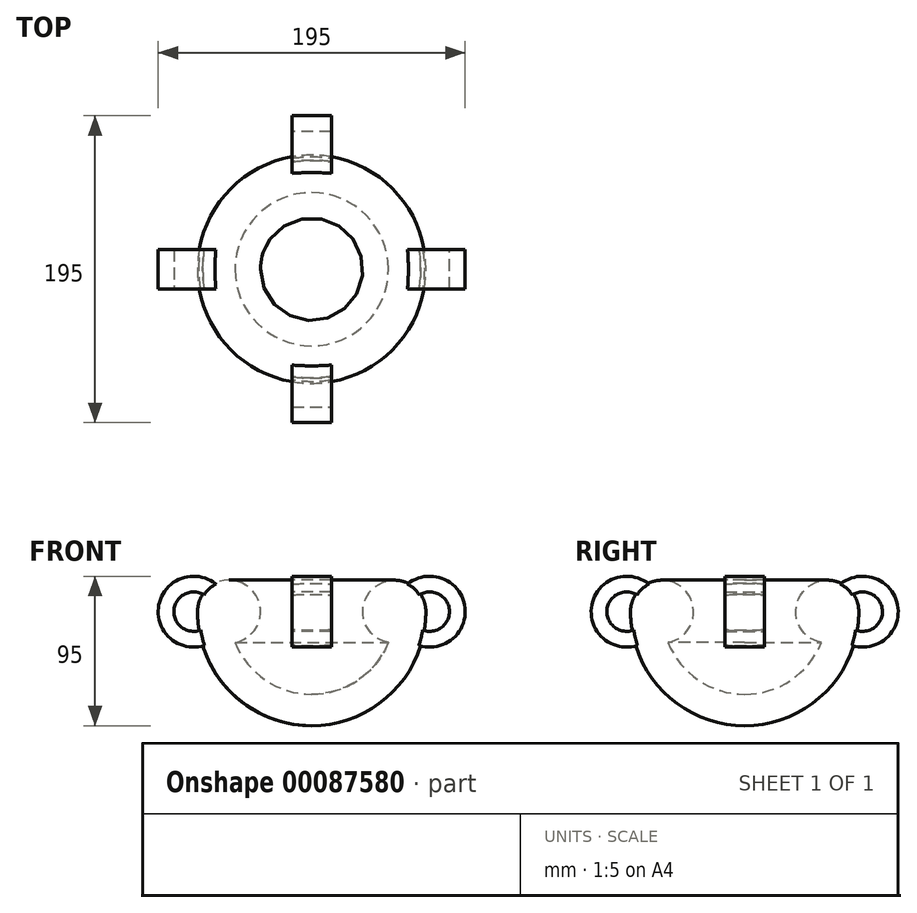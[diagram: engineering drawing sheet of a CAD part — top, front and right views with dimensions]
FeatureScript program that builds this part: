
annotation { "Feature Type Name" : "Feature", "Feature Type Description" : "" }
export const myFeature = defineFeature(function(context is Context, id is Id, definition is map)
    precondition{}
    {
        {
            var Q0;
            Q0=qCreatedBy(makeId("Front.planeOp"),FACE);
            var sketch = newSketch(context, id + "F0", { "sketchPlane" : qUnion([Q0])});
            skArc(sketch, "E0", {"start": v(72.5, 0) * mm, "mid": v(65.22, 15.43) * mm, "end": v(48.7, 19.63) * mm});
            skLineSegment(sketch, "E1", {"start": v(48.7, 19.63) * mm, "end": v(48.7, 19.63) * mm});
            skArc(sketch, "E2", {"start": v(72.5, 0) * mm, "mid": v(39.78, 15.43) * mm, "end": v(48.7, -19.63) * mm});
            skArc(sketch, "E3", {"start": v(0, -72.5) * mm, "mid": v(51.27, -51.27) * mm, "end": v(72.5, 0) * mm});
            skArc(sketch, "E4", {"start": v(0, -52.5) * mm, "mid": v(29.37, -43.51) * mm, "end": v(48.7, -19.63) * mm});
            skLineSegment(sketch, "E5", {"start": v(0, 72.5) * mm, "end": v(0, -72.5) * mm, "construction": true});
            skLineSegment(sketch, "E6", {"start": v(0, -52.5) * mm, "end": v(0, -72.5) * mm});
            skSolve(sketch);
        }
        {
            var Q0;
            {var subQ0=sQuery(id+"F0.wireOp",EDGE,"E3");Q0=makeQuery(id+"F0.imprint","IMPRINT",FACE,{"disambiguationData":[TD([[makeQuery(id+"F0.imprint","IMPRINT",EDGE,{"derivedFrom":subQ0}),1.0]])]});}
            var Q1;
            Q1=sQuery(id+"F0.wireOp",EDGE,"E5");
            revolve(context, id + "F1", {"entities" : qUnion([Q0]), "axis" : qUnion([Q1]), "revolveType" : RevolveType.FULL, "oppositeDirection" : true});
        }
        {
            var Q0;
            Q0=qCreatedBy(makeId("Right.planeOp"),FACE);
            var sketch = newSketch(context, id + "F2", { "sketchPlane" : qUnion([Q0])});
            skCircle(sketch, "E7", {"center": v(75, 0) * mm, "radius": 12.5 * mm});
            skCircle(sketch, "E8", {"center": v(75, 0) * mm, "radius": 22.5 * mm});
            skSolve(sketch);
        }
        {
            var Q0;
            Q0=makeQuery(id+"F2.imprint","IMPRINT",FACE,{"disambiguationData":[TD([[makeQuery(id+"F2.imprint","IMPRINT",EDGE,{"derivedFrom":sQuery(id+"F2.wireOp",EDGE,"E7")}),-1.0]])]});
            extrude(context, id + "F3", {"entities" : qUnion([Q0]), "endBound" : BoundingType.SYMMETRIC, "depth" : 25 * mm});
        }
        {
            var Q0;
            Q0=makeQuery(id+"F3.opExtrude","SWEPT_BODY",BODY,{"disambiguationData":[OSD([sQuery(id+"F2.wireOp",EDGE,"E7"),sQuery(id+"F2.wireOp",EDGE,"E8")])]});
            var Q1;
            Q1=sQuery(id+"F0.wireOp",EDGE,"E5");
            circularPattern(context, id + "F4", {"operationType" : NewBodyOperationType.ADD, "entities" : qUnion([Q0]), "axis" : qUnion([Q1]), "angle" : 90 * degree, "instanceCount" : 4});
        }
    });
